# Revit family: CENTUM Konsole XL100
name_source: partatom
category: HLS-Bauteile
revit_build: Autodesk Revit 2017 (Build: 20190508_0315(x64)
units: mm (PartAtom-declared; Revit-internal decimal feet)

## family parameters
Basisbauteil = Fläche
Beim Laden mit Abzugskörper schneiden = Nein
Bemaßung runder Anschluss = Durchmesser verwenden
Gemeinsam genutzt = Ja
Raumberechnungspunkt = Nein
Teiletyp = Normal

## types (3) — shared parameters
Breite Platte = 220 mm  [stored 0.721785 ft]
Breite Profil = 100 mm  [stored 0.328084 ft]
Fabrikat = MEFA
Firma = MEFA Befestigungs- und Montagesysteme GmbH
Höhe Profil = 100 mm  [stored 0.328084 ft]
Kurztext1 = Konsole Centum XL 100
Langloch Platte = 27x18 mm
Lochabstand = 150 mm
Länge Platte = 220 mm  [stored 0.721785 ft]
Material = Stahl
Materialname C-Profil = S235JR
Materialname Platte = S235JR
Oberflaeche = feuerstückverzinkt
Profil = CENTUM
Stärke Platte = 15 mm  [stored 0.0492126 ft]
Stärke Profil = 3 mm  [stored 0.00984252 ft]
Vorgabe-Ansicht = 1219 mm

## per-type parameters (varying)
| type | Artikelnummer | EAN | Gewicht | Gewicht pro Bauteil | Kurztext2 | Länge Konsole | Schienenlänge | max. zul. Last F1 | max. zul. Last F2 | max. zul. Last q0 |
| CENTUM Konsole XL100 L=1440 | 1631001440 | 4250928436795 | 18.02 kg | 18.02 kg | L= 1.440 mm fsv | 1 mm  [stored 0.00328084 ft] | CENTUM Profil XL100 für Konsole_ : CENTUM Profil XL100 L=1440 | 1.82 kip | 1.03 kip | 0.384 kip/ft |
| CENTUM Konsole XL100 L= 960 | 1631000960 | 4250928436788 | 13.62 kg | 13.62 kg | L= 960 mm fsv | 960 mm  [stored 3.14961 ft] | CENTUM Profil XL100 für Konsole_ : CENTUM Profil XL100 L= 960 | 2.73 kip | 1.36 kip | 0.865 kip/ft |
| CENTUM Konsole XL100 L= 720 | 1631000720 | 4250928436771 | 11.92 kg | 11.92 kg | L= 720 mm fsv | 720 mm  [stored 2.3622 ft] | CENTUM Profil XL100 für Konsole_ : CENTUM Profil XL100 L= 720 | 3.64 kip | 1.82 kip | 1.538 kip/ft |

note: [stored X ft] marks values corroborated as IEEE doubles in the binary element streams (Revit-internal decimal feet)
